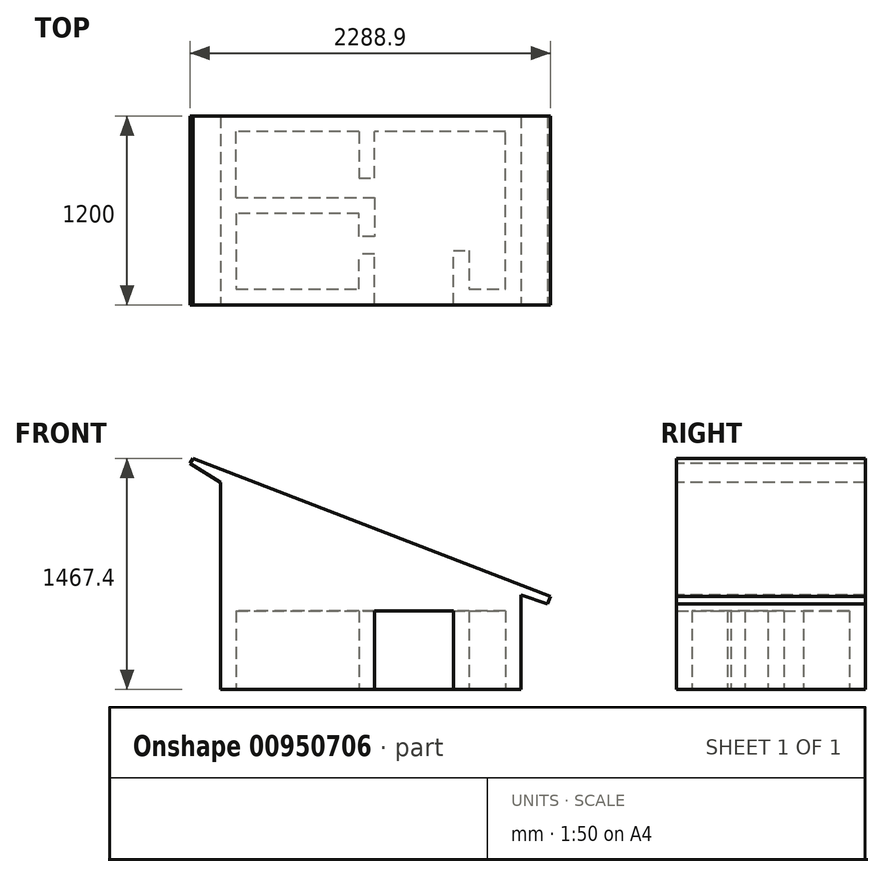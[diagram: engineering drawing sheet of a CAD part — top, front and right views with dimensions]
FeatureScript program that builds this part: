
annotation { "Feature Type Name" : "Feature", "Feature Type Description" : "" }
export const myFeature = defineFeature(function(context is Context, id is Id, definition is map)
    precondition{}
    {
        {
            var Q0;
            Q0=qCreatedBy(makeId("Top.planeOp"),FACE);
            var sketch = newSketch(context, id + "F0", { "sketchPlane" : qUnion([Q0])});
            skLineSegment(sketch, "E0", {"start": v(-939.48, -481.56) * mm, "end": v(-710.15, -481.56) * mm});
            skLineSegment(sketch, "E1", {"start": v(-160.38, -481.56) * mm, "end": v(-160.38, -258.33) * mm});
            skLineSegment(sketch, "E2", {"start": v(-160.38, -258.33) * mm, "end": v(-160.38, -145.85) * mm});
            skLineSegment(sketch, "E3", {"start": v(-160.38, -145.85) * mm, "end": v(-160.38, 0) * mm});
            skLineSegment(sketch, "E4", {"start": v(-160.38, 0) * mm, "end": v(-939.48, 0) * mm});
            skLineSegment(sketch, "E5", {"start": v(-939.48, 0) * mm, "end": v(-939.48, -481.56) * mm});
            skLineSegment(sketch, "E6", {"start": v(-939.48, 0) * mm, "end": v(-939.48, 100) * mm});
            skLineSegment(sketch, "E7", {"start": v(-939.48, 518.44) * mm, "end": v(-1039.48, 518.44) * mm});
            skLineSegment(sketch, "E8", {"start": v(-1039.48, 518.44) * mm, "end": v(-1039.48, -481.56) * mm});
            skLineSegment(sketch, "E9", {"start": v(-1039.48, -481.56) * mm, "end": v(-939.48, -481.56) * mm});
            skLineSegment(sketch, "E10", {"start": v(-939.48, 100) * mm, "end": v(-160.38, 100) * mm});
            skLineSegment(sketch, "E11", {"start": v(-160.38, 100) * mm, "end": v(-160.38, 0) * mm});
            skLineSegment(sketch, "E12", {"start": v(-160.38, 100) * mm, "end": v(-60.38, 100) * mm});
            skLineSegment(sketch, "E13", {"start": v(-60.38, 100) * mm, "end": v(-60.38, 100) * mm});
            skLineSegment(sketch, "E14", {"start": v(-60.38, -145.85) * mm, "end": v(-160.38, -145.85) * mm});
            skLineSegment(sketch, "E15", {"start": v(-1039.48, -481.56) * mm, "end": v(-1039.48, -581.56) * mm});
            skLineSegment(sketch, "E16", {"start": v(-1039.48, -581.56) * mm, "end": v(-710.15, -581.56) * mm});
            skLineSegment(sketch, "E17", {"start": v(-710.15, -581.56) * mm, "end": v(-710.15, -481.56) * mm});
            skLineSegment(sketch, "E18", {"start": v(-539.86, -481.56) * mm, "end": v(-539.86, -581.56) * mm});
            skLineSegment(sketch, "E19", {"start": v(-539.86, -581.56) * mm, "end": v(-160.38, -581.56) * mm});
            skLineSegment(sketch, "E20", {"start": v(-160.38, -581.56) * mm, "end": v(-160.38, -508.66) * mm});
            skLineSegment(sketch, "E21", {"start": v(-160.38, -581.56) * mm, "end": v(-60.38, -581.56) * mm});
            skLineSegment(sketch, "E22", {"start": v(-60.38, -581.56) * mm, "end": v(-60.38, -258.33) * mm});
            skLineSegment(sketch, "E23", {"start": v(-60.38, -258.33) * mm, "end": v(-160.38, -258.33) * mm});
            skLineSegment(sketch, "E24", {"start": v(-1039.48, 518.44) * mm, "end": v(-1039.48, 618.44) * mm});
            skLineSegment(sketch, "E25", {"start": v(-1039.48, 618.44) * mm, "end": v(-659.12, 618.44) * mm});
            skLineSegment(sketch, "E26", {"start": v(-60.38, 618.44) * mm, "end": v(-60.38, 518.44) * mm});
            skLineSegment(sketch, "E27", {"start": v(-60.38, 518.44) * mm, "end": v(-60.38, 518.44) * mm});
            skLineSegment(sketch, "E28", {"start": v(-160.38, 518.44) * mm, "end": v(-160.38, 225.84) * mm});
            skLineSegment(sketch, "E29", {"start": v(-160.38, 225.84) * mm, "end": v(-60.38, 225.84) * mm});
            skLineSegment(sketch, "E30", {"start": v(-60.38, 225.84) * mm, "end": v(-60.38, 518.44) * mm});
            skLineSegment(sketch, "E31", {"start": v(-81.43, 618.44) * mm, "end": v(-60.38, 618.44) * mm});
            skLineSegment(sketch, "E32", {"start": v(335.04, 618.44) * mm, "end": v(335.04, 518.44) * mm});
            skLineSegment(sketch, "E33", {"start": v(335.04, 518.44) * mm, "end": v(-60.38, 518.44) * mm});
            skLineSegment(sketch, "E34", {"start": v(335.04, 618.44) * mm, "end": v(523.5, 618.44) * mm});
            skLineSegment(sketch, "E35", {"start": v(523.5, 618.44) * mm, "end": v(523.5, 518.44) * mm});
            skLineSegment(sketch, "E36", {"start": v(523.5, 518.44) * mm, "end": v(335.04, 518.44) * mm});
            skLineSegment(sketch, "E37", {"start": v(523.5, 618.44) * mm, "end": v(870.93, 618.44) * mm});
            skLineSegment(sketch, "E38", {"start": v(870.93, 618.44) * mm, "end": v(870.93, 618.44) * mm});
            skLineSegment(sketch, "E39", {"start": v(870.93, 518.44) * mm, "end": v(770.93, 518.44) * mm});
            skLineSegment(sketch, "E40", {"start": v(870.93, 518.44) * mm, "end": v(870.93, 156.86) * mm});
            skLineSegment(sketch, "E41", {"start": v(870.93, 156.86) * mm, "end": v(770.93, 156.86) * mm});
            skLineSegment(sketch, "E42", {"start": v(770.93, 156.86) * mm, "end": v(770.93, 518.44) * mm});
            skLineSegment(sketch, "E43", {"start": v(870.93, 156.86) * mm, "end": v(870.93, 156.86) * mm});
            skLineSegment(sketch, "E44", {"start": v(870.93, 0) * mm, "end": v(770.93, 0) * mm});
            skLineSegment(sketch, "E45", {"start": v(770.93, 0) * mm, "end": v(770.93, 156.86) * mm});
            skLineSegment(sketch, "E46", {"start": v(770.93, 0) * mm, "end": v(770.93, -152.86) * mm});
            skLineSegment(sketch, "E47", {"start": v(770.93, -152.86) * mm, "end": v(770.93, -152.86) * mm});
            skLineSegment(sketch, "E48", {"start": v(870.93, -170.47) * mm, "end": v(870.93, -152.86) * mm});
            skLineSegment(sketch, "E49", {"start": v(870.93, -152.86) * mm, "end": v(870.93, -581.56) * mm});
            skLineSegment(sketch, "E50", {"start": v(870.93, -581.56) * mm, "end": v(770.93, -581.56) * mm});
            skLineSegment(sketch, "E51", {"start": v(770.93, -581.56) * mm, "end": v(770.93, -481.56) * mm});
            skLineSegment(sketch, "E52", {"start": v(770.93, -581.56) * mm, "end": v(770.93, -581.56) * mm});
            skLineSegment(sketch, "E53", {"start": v(439.62, -581.56) * mm, "end": v(439.62, -581.56) * mm});
            skLineSegment(sketch, "E54", {"start": v(439.62, -499.17) * mm, "end": v(439.62, -481.56) * mm});
            skLineSegment(sketch, "E55", {"start": v(439.62, -236.35) * mm, "end": v(439.62, -236.35) * mm});
            skLineSegment(sketch, "E56", {"start": v(539.62, -236.35) * mm, "end": v(539.62, -236.35) * mm});
            skLineSegment(sketch, "E57", {"start": v(-710.15, -581.56) * mm, "end": v(-539.86, -581.56) * mm});
            skLineSegment(sketch, "E58", {"start": v(-60.38, -581.56) * mm, "end": v(439.62, -581.56) * mm});
            skLineSegment(sketch, "E59", {"start": v(-659.12, 618.44) * mm, "end": v(-659.12, 518.44) * mm});
            skLineSegment(sketch, "E60", {"start": v(-436.97, 618.44) * mm, "end": v(-436.97, 518.44) * mm});
            skLineSegment(sketch, "E61", {"start": v(-939.48, 518.44) * mm, "end": v(-939.48, 518.44) * mm});
            skLineSegment(sketch, "E62", {"start": v(-659.12, 518.44) * mm, "end": v(-939.48, 518.44) * mm});
            skLineSegment(sketch, "E63", {"start": v(-436.97, 518.44) * mm, "end": v(-659.12, 518.44) * mm});
            skLineSegment(sketch, "E64", {"start": v(-160.38, 0) * mm, "end": v(-160.38, 0) * mm});
            skLineSegment(sketch, "E65", {"start": v(-60.38, 100) * mm, "end": v(-60.38, -145.85) * mm});
            skLineSegment(sketch, "E66", {"start": v(-60.38, -145.85) * mm, "end": v(-60.38, -145.85) * mm});
            skLineSegment(sketch, "E67", {"start": v(-160.38, 518.44) * mm, "end": v(-436.97, 518.44) * mm});
            skLineSegment(sketch, "E68", {"start": v(-60.38, 518.44) * mm, "end": v(-160.38, 518.44) * mm});
            skLineSegment(sketch, "E69", {"start": v(-81.43, 618.44) * mm, "end": v(335.04, 618.44) * mm});
            skLineSegment(sketch, "E70", {"start": v(770.93, 518.44) * mm, "end": v(770.93, 518.44) * mm});
            skLineSegment(sketch, "E71", {"start": v(770.93, 156.86) * mm, "end": v(770.93, 156.86) * mm});
            skLineSegment(sketch, "E72", {"start": v(770.93, 0) * mm, "end": v(770.93, 0) * mm});
            skLineSegment(sketch, "E73", {"start": v(870.93, 618.44) * mm, "end": v(870.93, 518.44) * mm});
            skLineSegment(sketch, "E74", {"start": v(870.93, 156.86) * mm, "end": v(870.93, 0) * mm});
            skLineSegment(sketch, "E75", {"start": v(870.93, 0) * mm, "end": v(870.93, 0) * mm});
            skLineSegment(sketch, "E76", {"start": v(870.93, -170.47) * mm, "end": v(870.93, 0) * mm});
            skLineSegment(sketch, "E77", {"start": v(770.93, -152.86) * mm, "end": v(870.93, -152.86) * mm});
            skLineSegment(sketch, "E78", {"start": v(770.93, -481.56) * mm, "end": v(770.93, -152.86) * mm});
            skLineSegment(sketch, "E79", {"start": v(539.62, -236.35) * mm, "end": v(539.62, -481.56) * mm});
            skLineSegment(sketch, "E80", {"start": v(439.62, -236.35) * mm, "end": v(539.62, -236.35) * mm});
            skLineSegment(sketch, "E81", {"start": v(-60.38, -581.56) * mm, "end": v(-60.38, -581.56) * mm});
            skLineSegment(sketch, "E82", {"start": v(-60.38, -258.33) * mm, "end": v(-60.38, -258.33) * mm});
            skLineSegment(sketch, "E83", {"start": v(-160.38, -508.66) * mm, "end": v(-160.38, -481.56) * mm});
            skLineSegment(sketch, "E84", {"start": v(-539.86, -481.56) * mm, "end": v(-160.38, -481.56) * mm});
            skLineSegment(sketch, "E85", {"start": v(-710.15, -481.56) * mm, "end": v(-539.86, -481.56) * mm});
            skLineSegment(sketch, "E86", {"start": v(-659.12, 618.44) * mm, "end": v(-436.97, 618.44) * mm});
            skLineSegment(sketch, "E87", {"start": v(-436.97, 618.44) * mm, "end": v(-60.38, 618.44) * mm});
            skLineSegment(sketch, "E88", {"start": v(439.62, -499.17) * mm, "end": v(439.62, -236.35) * mm});
            skLineSegment(sketch, "E89", {"start": v(439.62, -581.56) * mm, "end": v(439.62, -499.17) * mm});
            skLineSegment(sketch, "E90", {"start": v(770.93, -581.56) * mm, "end": v(439.62, -581.56) * mm});
            skLineSegment(sketch, "E91", {"start": v(770.93, 518.44) * mm, "end": v(523.5, 518.44) * mm});
            skLineSegment(sketch, "E92", {"start": v(539.62, -481.56) * mm, "end": v(770.93, -481.56) * mm});
            skLineSegment(sketch, "E93", {"start": v(-939.48, 100) * mm, "end": v(-939.48, 518.44) * mm});
            skSolve(sketch);
        }
        {
            var Q0;
            Q0=makeQuery(id+"F0.imprint","IMPRINT",FACE,{"disambiguationData":[TD([[makeQuery(id+"F0.imprint","IMPRINT",EDGE,{"derivedFrom":sQuery(id+"F0.wireOp",EDGE,"E5")}),-1.0]])]});
            var Q1;
            Q1=makeQuery(id+"F0.imprint","IMPRINT",FACE,{"disambiguationData":[TD([[makeQuery(id+"F0.imprint","IMPRINT",EDGE,{"derivedFrom":sQuery(id+"F0.wireOp",EDGE,"E0")}),-1.0]])]});
            var Q2;
            Q2=makeQuery(id+"F0.imprint","IMPRINT",FACE,{"disambiguationData":[TD([[makeQuery(id+"F0.imprint","IMPRINT",EDGE,{"derivedFrom":sQuery(id+"F0.wireOp",EDGE,"E7")}),-1.0]])]});
            var Q3;
            Q3=makeQuery(id+"F0.imprint","IMPRINT",FACE,{"disambiguationData":[TD([[makeQuery(id+"F0.imprint","IMPRINT",EDGE,{"derivedFrom":sQuery(id+"F0.wireOp",EDGE,"E59")}),1.0]])]});
            var Q4;
            {var subQ1=sQuery(id+"F0.wireOp",EDGE,"E26");Q4=makeQuery(id+"F0.imprint","IMPRINT",FACE,{"disambiguationData":[TD([[makeQuery(id+"F0.imprint","IMPRINT",EDGE,{"derivedFrom":subQ1}),-1.0]])]});}
            var Q5;
            Q5=makeQuery(id+"F0.imprint","IMPRINT",FACE,{"disambiguationData":[TD([[makeQuery(id+"F0.imprint","IMPRINT",EDGE,{"derivedFrom":sQuery(id+"F0.wireOp",EDGE,"E26")}),1.0]])]});
            var Q6;
            Q6=makeQuery(id+"F0.imprint","IMPRINT",FACE,{"disambiguationData":[TD([[makeQuery(id+"F0.imprint","IMPRINT",EDGE,{"derivedFrom":sQuery(id+"F0.wireOp",EDGE,"E32")}),1.0]])]});
            var Q7;
            Q7=makeQuery(id+"F0.imprint","IMPRINT",FACE,{"disambiguationData":[TD([[makeQuery(id+"F0.imprint","IMPRINT",EDGE,{"derivedFrom":sQuery(id+"F0.wireOp",EDGE,"E35")}),1.0]])]});
            var Q8;
            Q8=makeQuery(id+"F0.imprint","IMPRINT",FACE,{"disambiguationData":[TD([[makeQuery(id+"F0.imprint","IMPRINT",EDGE,{"derivedFrom":sQuery(id+"F0.wireOp",EDGE,"E39")}),1.0]])]});
            var Q9;
            Q9=makeQuery(id+"F0.imprint","IMPRINT",FACE,{"disambiguationData":[TD([[makeQuery(id+"F0.imprint","IMPRINT",EDGE,{"derivedFrom":sQuery(id+"F0.wireOp",EDGE,"E41")}),1.0]])]});
            var Q10;
            {var subQ0=sQuery(id+"F0.wireOp",EDGE,"E44");Q10=makeQuery(id+"F0.imprint","IMPRINT",FACE,{"disambiguationData":[TD([[makeQuery(id+"F0.imprint","IMPRINT",EDGE,{"derivedFrom":subQ0}),1.0]])]});}
            var Q11;
            {var subQ1=sQuery(id+"F0.wireOp",EDGE,"E49");Q11=makeQuery(id+"F0.imprint","IMPRINT",FACE,{"disambiguationData":[TD([[makeQuery(id+"F0.imprint","IMPRINT",EDGE,{"derivedFrom":subQ1}),-1.0]])]});}
            var Q12;
            Q12=makeQuery(id+"F0.imprint","IMPRINT",FACE,{"disambiguationData":[TD([[makeQuery(id+"F0.imprint","IMPRINT",EDGE,{"derivedFrom":sQuery(id+"F0.wireOp",EDGE,"E51")}),1.0]])]});
            var Q13;
            Q13=makeQuery(id+"F0.imprint","IMPRINT",FACE,{"disambiguationData":[TD([[makeQuery(id+"F0.imprint","IMPRINT",EDGE,{"derivedFrom":sQuery(id+"F0.wireOp",EDGE,"E1")}),-1.0]])]});
            var Q14;
            Q14=makeQuery(id+"F0.imprint","IMPRINT",FACE,{"disambiguationData":[TD([[makeQuery(id+"F0.imprint","IMPRINT",EDGE,{"derivedFrom":sQuery(id+"F0.wireOp",EDGE,"E17")}),-1.0]])]});
            var Q15;
            Q15=makeQuery(id+"F0.imprint","IMPRINT",FACE,{"disambiguationData":[TD([[makeQuery(id+"F0.imprint","IMPRINT",EDGE,{"derivedFrom":sQuery(id+"F0.wireOp",EDGE,"E4")}),-1.0]])]});
            var Q16;
            Q16=makeQuery(id+"F0.imprint","IMPRINT",FACE,{"disambiguationData":[TD([[makeQuery(id+"F0.imprint","IMPRINT",EDGE,{"derivedFrom":sQuery(id+"F0.wireOp",EDGE,"E18")}),1.0]])]});
            var Q17;
            Q17=makeQuery(id+"F0.imprint","IMPRINT",FACE,{"disambiguationData":[TD([[makeQuery(id+"F0.imprint","IMPRINT",EDGE,{"derivedFrom":sQuery(id+"F0.wireOp",EDGE,"E3")}),-1.0]])]});
            var Q18;
            Q18=makeQuery(id+"F0.imprint","IMPRINT",FACE,{"disambiguationData":[TD([[makeQuery(id+"F0.imprint","IMPRINT",EDGE,{"derivedFrom":sQuery(id+"F0.wireOp",EDGE,"E28")}),1.0]])]});
            extrude(context, id + "F1", {"entities" : qUnion([Q0, Q1, Q2, Q3, Q4, Q5, Q6, Q7, Q8, Q9, Q10, Q11, Q12, Q13, Q14, Q15, Q16, Q17, Q18]), "depth" : 500 * mm, "offsetDistance" : 25 * mm});
        }
        {
            var Q0;
            Q0=makeQuery(id+"F1.opExtrude","CAP_FACE",FACE,{"disambiguationData":[OSD([sQuery(id+"F0.wireOp",EDGE,"E0"),sQuery(id+"F0.wireOp",EDGE,"E1"),sQuery(id+"F0.wireOp",EDGE,"E3"),sQuery(id+"F0.wireOp",EDGE,"E4"),sQuery(id+"F0.wireOp",EDGE,"E5"),sQuery(id+"F0.wireOp",EDGE,"E8"),sQuery(id+"F0.wireOp",EDGE,"E10"),sQuery(id+"F0.wireOp",EDGE,"E12"),sQuery(id+"F0.wireOp",EDGE,"E14"),sQuery(id+"F0.wireOp",EDGE,"E15"),sQuery(id+"F0.wireOp",EDGE,"E16"),sQuery(id+"F0.wireOp",EDGE,"E19"),sQuery(id+"F0.wireOp",EDGE,"E21"),sQuery(id+"F0.wireOp",EDGE,"E22"),sQuery(id+"F0.wireOp",EDGE,"E23"),sQuery(id+"F0.wireOp",EDGE,"E24"),sQuery(id+"F0.wireOp",EDGE,"E25"),sQuery(id+"F0.wireOp",EDGE,"E28"),sQuery(id+"F0.wireOp",EDGE,"E29"),sQuery(id+"F0.wireOp",EDGE,"E30"),sQuery(id+"F0.wireOp",EDGE,"E33"),sQuery(id+"F0.wireOp",EDGE,"E34"),sQuery(id+"F0.wireOp",EDGE,"E36"),sQuery(id+"F0.wireOp",EDGE,"E37"),sQuery(id+"F0.wireOp",EDGE,"E40"),sQuery(id+"F0.wireOp",EDGE,"E42"),sQuery(id+"F0.wireOp",EDGE,"E45"),sQuery(id+"F0.wireOp",EDGE,"E46"),sQuery(id+"F0.wireOp",EDGE,"E49"),sQuery(id+"F0.wireOp",EDGE,"E50"),sQuery(id+"F0.wireOp",EDGE,"E57"),sQuery(id+"F0.wireOp",EDGE,"E62"),sQuery(id+"F0.wireOp",EDGE,"E63"),sQuery(id+"F0.wireOp",EDGE,"E65"),sQuery(id+"F0.wireOp",EDGE,"E67"),sQuery(id+"F0.wireOp",EDGE,"E69"),sQuery(id+"F0.wireOp",EDGE,"E73"),sQuery(id+"F0.wireOp",EDGE,"E74"),sQuery(id+"F0.wireOp",EDGE,"E76"),sQuery(id+"F0.wireOp",EDGE,"E78"),sQuery(id+"F0.wireOp",EDGE,"E79"),sQuery(id+"F0.wireOp",EDGE,"E80"),sQuery(id+"F0.wireOp",EDGE,"E84"),sQuery(id+"F0.wireOp",EDGE,"E85"),sQuery(id+"F0.wireOp",EDGE,"E86"),sQuery(id+"F0.wireOp",EDGE,"E87"),sQuery(id+"F0.wireOp",EDGE,"E88"),sQuery(id+"F0.wireOp",EDGE,"E89"),sQuery(id+"F0.wireOp",EDGE,"E90"),sQuery(id+"F0.wireOp",EDGE,"E91"),sQuery(id+"F0.wireOp",EDGE,"E92"),sQuery(id+"F0.wireOp",EDGE,"E93")])],"isStart":false});
            var sketch = newSketch(context, id + "F2", { "sketchPlane" : qUnion([Q0])});
            skLineSegment(sketch, "E94.bottom", {"start": v(-1039.48, 618.44) * mm, "end": v(870.93, 618.44) * mm});
            skLineSegment(sketch, "E94.top", {"start": v(-1039.48, -581.56) * mm, "end": v(870.93, -581.56) * mm});
            skLineSegment(sketch, "E94.left", {"start": v(-1039.48, 618.44) * mm, "end": v(-1039.48, -581.56) * mm});
            skLineSegment(sketch, "E94.right", {"start": v(870.93, 618.44) * mm, "end": v(870.93, -581.56) * mm});
            skSolve(sketch);
        }
        {
            var Q0;
            Q0 = qSketchRegion(id + "F2", true);
            extrude(context, id + "F3", {"entities" : qUnion([Q0]), "operationType" : NewBodyOperationType.ADD, "depth" : 100 * mm, "offsetDistance" : 25 * mm});
        }
        {
            var Q0;
            Q0=makeQuery(id+"F3.boolean.opBoolean","MERGE",FACE,{"derivedFrom":[makeQuery(id+"F1.opExtrude","SWEPT_FACE",FACE,{"disambiguationData":[OSD([sQuery(id+"F0.wireOp",EDGE,"E16"),sQuery(id+"F0.wireOp",EDGE,"E19"),sQuery(id+"F0.wireOp",EDGE,"E21"),sQuery(id+"F0.wireOp",EDGE,"E57")])]}),makeQuery(id+"F1.opExtrude","SWEPT_FACE",FACE,{"disambiguationData":[OSD([sQuery(id+"F0.wireOp",EDGE,"E50"),sQuery(id+"F0.wireOp",EDGE,"E90")])]}),makeQuery(id+"F3.opExtrude","SWEPT_FACE",FACE,{"disambiguationData":[OSD([sQuery(id+"F2.wireOp",EDGE,"E94.top")])]})]});
            var sketch = newSketch(context, id + "F4", { "sketchPlane" : qUnion([Q0])});
            skLineSegment(sketch, "E95", {"start": v(-1039.48, 600) * mm, "end": v(-1039.48, 1188.94) * mm});
            skLineSegment(sketch, "E96", {"start": v(-1039.48, 1188.94) * mm, "end": v(-1039.48, 1314.15) * mm});
            skLineSegment(sketch, "E97", {"start": v(-1039.48, 1314.15) * mm, "end": v(-1231.85, 1435.44) * mm});
            skLineSegment(sketch, "E98", {"start": v(-1231.85, 1435.44) * mm, "end": v(-1211.7, 1467.4) * mm});
            skLineSegment(sketch, "E99", {"start": v(-1211.7, 1467.4) * mm, "end": v(1057.05, 592.26) * mm});
            skLineSegment(sketch, "E100", {"start": v(1057.05, 592.26) * mm, "end": v(1038.45, 544.05) * mm});
            skLineSegment(sketch, "E101", {"start": v(1038.45, 544.05) * mm, "end": v(870.93, 600) * mm});
            skLineSegment(sketch, "E102", {"start": v(870.93, 600) * mm, "end": v(-1039.48, 600) * mm});
            skSolve(sketch);
        }
        {
            var Q0;
            Q0=makeQuery(id+"F4.imprint","IMPRINT",FACE,{"disambiguationData":[TD([[makeQuery(id+"F4.imprint","IMPRINT",EDGE,{"derivedFrom":sQuery(id+"F4.wireOp",EDGE,"E95")}),-1.0]])]});
            extrude(context, id + "F5", {"entities" : qUnion([Q0]), "operationType" : NewBodyOperationType.ADD, "oppositeDirection" : true, "depth" : 1200 * mm, "offsetDistance" : 25 * mm});
        }
    });
